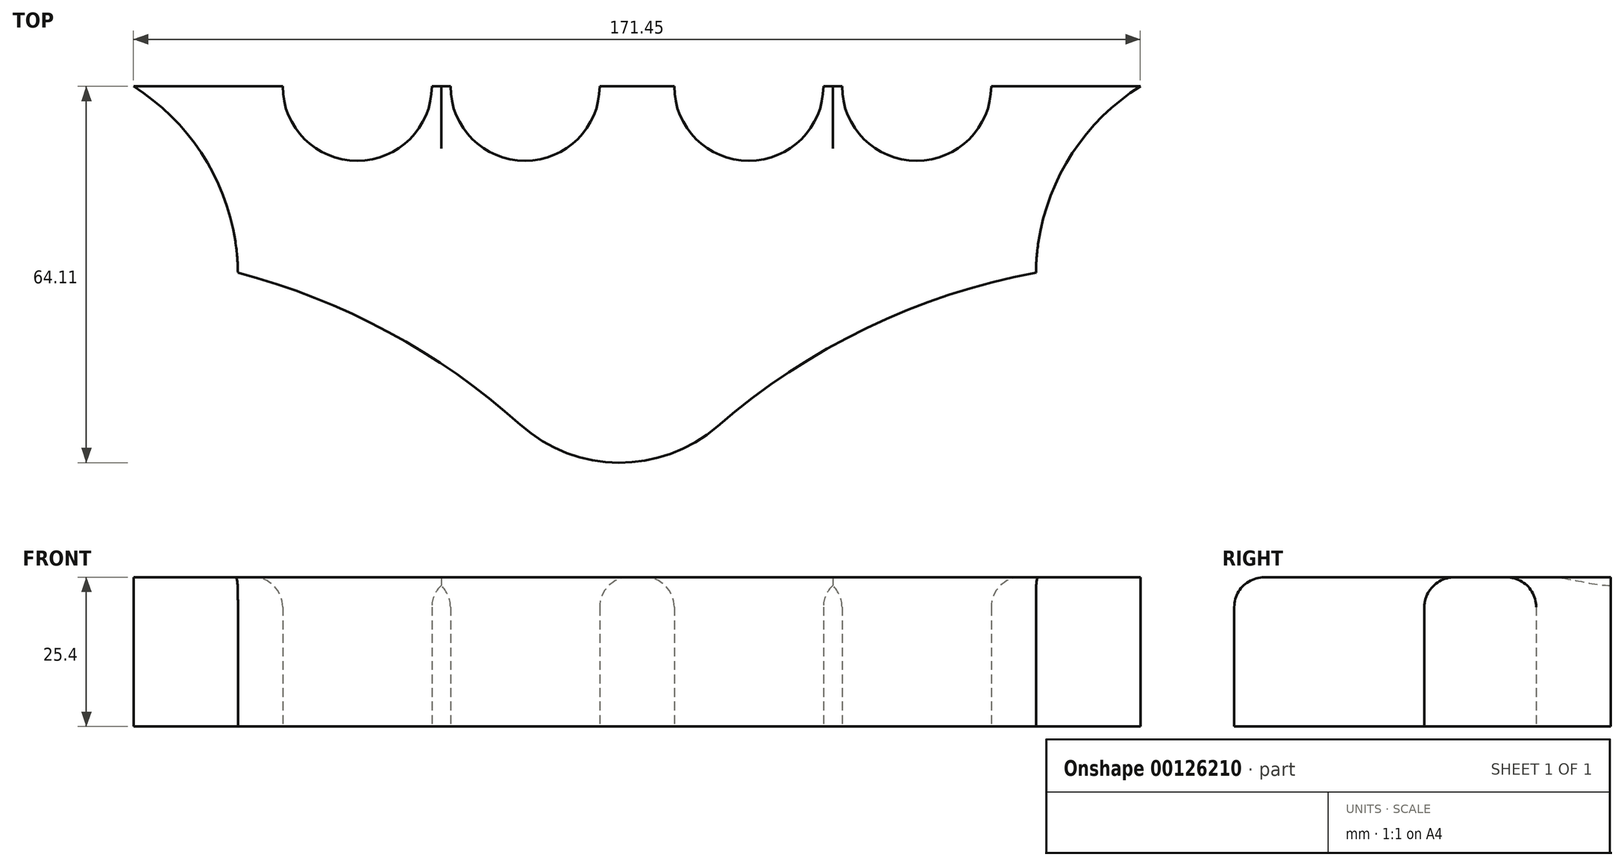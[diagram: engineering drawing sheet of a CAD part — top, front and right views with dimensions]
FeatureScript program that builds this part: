
annotation { "Feature Type Name" : "Feature", "Feature Type Description" : "" }
export const myFeature = defineFeature(function(context is Context, id is Id, definition is map)
    precondition{}
    {
        {
            var Q0;
            Q0=qCreatedBy(makeId("Top.planeOp"),FACE);
            var sketch = newSketch(context, id + "F0", { "sketchPlane" : qUnion([Q0])});
            skLineSegment(sketch, "E0", {"start": v(11.71, 92.4) * mm, "end": v(37.11, 92.4) * mm});
            skLineSegment(sketch, "E1", {"start": v(157.76, 92.4) * mm, "end": v(183.16, 92.4) * mm});
            skLineSegment(sketch, "E2", {"start": v(62.51, 92.4) * mm, "end": v(65.69, 92.4) * mm});
            skLineSegment(sketch, "E3", {"start": v(91.09, 92.4) * mm, "end": v(103.79, 92.4) * mm});
            skLineSegment(sketch, "E4", {"start": v(129.19, 92.4) * mm, "end": v(132.36, 92.4) * mm});
            skArc(sketch, "E5", {"start": v(37.11, 92.4) * mm, "mid": v(49.81, 79.7) * mm, "end": v(62.51, 92.4) * mm});
            skArc(sketch, "E6", {"start": v(65.69, 92.4) * mm, "mid": v(78.39, 79.7) * mm, "end": v(91.09, 92.4) * mm});
            skArc(sketch, "E7", {"start": v(103.79, 92.4) * mm, "mid": v(116.49, 79.7) * mm, "end": v(129.19, 92.4) * mm});
            skArc(sketch, "E8", {"start": v(132.36, 92.4) * mm, "mid": v(145.06, 79.7) * mm, "end": v(157.76, 92.4) * mm});
            skArc(sketch, "E9", {"start": v(29.5, 60.64) * mm, "mid": v(24.64, 78.78) * mm, "end": v(11.71, 92.4) * mm});
            skArc(sketch, "E10", {"start": v(94.26, 16.2) * mm, "mid": v(65.75, 44.06) * mm, "end": v(29.5, 60.64) * mm});
            skArc(sketch, "E11", {"start": v(183.16, 92.4) * mm, "mid": v(170.24, 78.78) * mm, "end": v(165.38, 60.64) * mm});
            skArc(sketch, "E12", {"start": v(165.38, 60.64) * mm, "mid": v(125.6, 45.18) * mm, "end": v(94.26, 16.2) * mm});
            skSolve(sketch);
        }
        {
            var Q0;
            Q0=makeQuery(id+"F0.imprint","IMPRINT",FACE,{"disambiguationData":[TD([[makeQuery(id+"F0.imprint","IMPRINT",EDGE,{"derivedFrom":sQuery(id+"F0.wireOp",EDGE,"E0")}),-1.0]])]});
            extrude(context, id + "F1", {"entities" : qUnion([Q0]), "depth" : 25.4 * mm});
        }
        {
            var Q0;
            Q0=makeQuery(id+"F1.opExtrude","SWEPT_EDGE",EDGE,{"disambiguationData":[OSD([sQuery(id+"F0.wireOp",EDGE,"E10"),sQuery(id+"F0.wireOp",EDGE,"E12")])]});
            fillet(context, id + "F2", {"entities" : qUnion([Q0]), "radius" : 25.4 * mm, "tangentPropagation" : true, "allowEdgeOverflow" : false});
        }
        {
            var Q0;
            Q0=makeQuery(id+"F1.opExtrude","CAP_EDGE",EDGE,{"disambiguationData":[OSD([sQuery(id+"F0.wireOp",EDGE,"E5")])],"isStart":false});
            var Q1;
            Q1=makeQuery(id+"F1.opExtrude","CAP_EDGE",EDGE,{"disambiguationData":[OSD([sQuery(id+"F0.wireOp",EDGE,"E7")])],"isStart":false});
            var Q2;
            Q2=makeQuery(id+"F1.opExtrude","CAP_EDGE",EDGE,{"disambiguationData":[OSD([sQuery(id+"F0.wireOp",EDGE,"E8")])],"isStart":false});
            var Q3;
            Q3=makeQuery(id+"F1.opExtrude","CAP_EDGE",EDGE,{"disambiguationData":[OSD([sQuery(id+"F0.wireOp",EDGE,"E6")])],"isStart":false});
            fillet(context, id + "F3", {"entities" : qUnion([Q0, Q1, Q2, Q3]), "radius" : 5.08 * mm, "tangentPropagation" : true, "allowEdgeOverflow" : false});
        }
        {
            var Q0;
            {var subQ0=sQuery(id+"F0.wireOp",EDGE,"E12");var subQ1=sQuery(id+"F0.wireOp",EDGE,"E10");Q0=makeQuery(id+"F2.opFillet","BLEND_EDGE",EDGE,{"blendedFrom":[makeQuery(id+"F1.opExtrude","SWEPT_EDGE",EDGE,{"disambiguationData":[OSD([subQ1,subQ0])]}),makeQuery(id+"F1.opExtrude","CAP_FACE",FACE,{"disambiguationData":[OSD([sQuery(id+"F0.wireOp",EDGE,"E0"),sQuery(id+"F0.wireOp",EDGE,"E1"),sQuery(id+"F0.wireOp",EDGE,"E2"),sQuery(id+"F0.wireOp",EDGE,"E3"),sQuery(id+"F0.wireOp",EDGE,"E4"),sQuery(id+"F0.wireOp",EDGE,"E5"),sQuery(id+"F0.wireOp",EDGE,"E6"),sQuery(id+"F0.wireOp",EDGE,"E7"),sQuery(id+"F0.wireOp",EDGE,"E8"),sQuery(id+"F0.wireOp",EDGE,"E9"),subQ1,sQuery(id+"F0.wireOp",EDGE,"E11"),subQ0])],"isStart":false})],"blendedInto":[makeQuery(id+"F1.opExtrude","CAP_FACE",FACE,{"disambiguationData":[OSD([sQuery(id+"F0.wireOp",EDGE,"E0"),sQuery(id+"F0.wireOp",EDGE,"E1"),sQuery(id+"F0.wireOp",EDGE,"E2"),sQuery(id+"F0.wireOp",EDGE,"E3"),sQuery(id+"F0.wireOp",EDGE,"E4"),sQuery(id+"F0.wireOp",EDGE,"E5"),sQuery(id+"F0.wireOp",EDGE,"E6"),sQuery(id+"F0.wireOp",EDGE,"E7"),sQuery(id+"F0.wireOp",EDGE,"E8"),sQuery(id+"F0.wireOp",EDGE,"E9"),subQ1,sQuery(id+"F0.wireOp",EDGE,"E11"),subQ0])],"isStart":false})]});}
            fillet(context, id + "F4", {"entities" : qUnion([Q0]), "radius" : 5.08 * mm, "tangentPropagation" : true, "allowEdgeOverflow" : false});
        }
        {
            var Q0;
            Q0=makeQuery(id+"F1.opExtrude","SWEPT_BODY",BODY,{"disambiguationData":[OSD([sQuery(id+"F0.wireOp",EDGE,"E0"),sQuery(id+"F0.wireOp",EDGE,"E1"),sQuery(id+"F0.wireOp",EDGE,"E2"),sQuery(id+"F0.wireOp",EDGE,"E3"),sQuery(id+"F0.wireOp",EDGE,"E4"),sQuery(id+"F0.wireOp",EDGE,"E5"),sQuery(id+"F0.wireOp",EDGE,"E6"),sQuery(id+"F0.wireOp",EDGE,"E7"),sQuery(id+"F0.wireOp",EDGE,"E8"),sQuery(id+"F0.wireOp",EDGE,"E9"),sQuery(id+"F0.wireOp",EDGE,"E10"),sQuery(id+"F0.wireOp",EDGE,"E11"),sQuery(id+"F0.wireOp",EDGE,"E12")])]});
            transform(context, id + "F5", {"entities" : qUnion([Q0]), "transformType" : TransformType.COPY});
        }
        {
            var Q0;
            Q0=makeQuery(id+"F5.opPattern","COPY",BODY,{"derivedFrom":makeQuery(id+"F1.opExtrude","SWEPT_BODY",BODY,{"disambiguationData":[OSD([sQuery(id+"F0.wireOp",EDGE,"E0"),sQuery(id+"F0.wireOp",EDGE,"E1"),sQuery(id+"F0.wireOp",EDGE,"E2"),sQuery(id+"F0.wireOp",EDGE,"E3"),sQuery(id+"F0.wireOp",EDGE,"E4"),sQuery(id+"F0.wireOp",EDGE,"E5"),sQuery(id+"F0.wireOp",EDGE,"E6"),sQuery(id+"F0.wireOp",EDGE,"E7"),sQuery(id+"F0.wireOp",EDGE,"E8"),sQuery(id+"F0.wireOp",EDGE,"E9"),sQuery(id+"F0.wireOp",EDGE,"E10"),sQuery(id+"F0.wireOp",EDGE,"E11"),sQuery(id+"F0.wireOp",EDGE,"E12")])]}),"instanceName":"1"});
            var Q1;
            Q1=makeQuery(id+"F0.imprint","IMPRINT",FACE,{"disambiguationData":[TD([[makeQuery(id+"F0.imprint","IMPRINT",EDGE,{"derivedFrom":sQuery(id+"F0.wireOp",EDGE,"E0")}),-1.0]])]});
            transform(context, id + "F6", {"entities" : qUnion([Q0]), "transformType" : TransformType.TRANSLATION_DISTANCE, "transformDirection" : qUnion([Q1]), "distance" : 50.8 * mm, "oppositeDirection" : true, "makeCopy" : true});
        }
        {
            var Q0;
            Q0=makeQuery(id+"F5.opPattern","COPY",BODY,{"derivedFrom":makeQuery(id+"F1.opExtrude","SWEPT_BODY",BODY,{"disambiguationData":[OSD([sQuery(id+"F0.wireOp",EDGE,"E0"),sQuery(id+"F0.wireOp",EDGE,"E1"),sQuery(id+"F0.wireOp",EDGE,"E2"),sQuery(id+"F0.wireOp",EDGE,"E3"),sQuery(id+"F0.wireOp",EDGE,"E4"),sQuery(id+"F0.wireOp",EDGE,"E5"),sQuery(id+"F0.wireOp",EDGE,"E6"),sQuery(id+"F0.wireOp",EDGE,"E7"),sQuery(id+"F0.wireOp",EDGE,"E8"),sQuery(id+"F0.wireOp",EDGE,"E9"),sQuery(id+"F0.wireOp",EDGE,"E10"),sQuery(id+"F0.wireOp",EDGE,"E11"),sQuery(id+"F0.wireOp",EDGE,"E12")])]}),"instanceName":"1"});
            deleteBodies(context, id + "F7", {"entities" : qUnion([Q0])});
        }
        {
            var Q0;
            Q0=makeQuery(id+"F6.opPattern","COPY",BODY,{"derivedFrom":makeQuery(id+"F5.opPattern","COPY",BODY,{"derivedFrom":makeQuery(id+"F1.opExtrude","SWEPT_BODY",BODY,{"disambiguationData":[OSD([sQuery(id+"F0.wireOp",EDGE,"E0"),sQuery(id+"F0.wireOp",EDGE,"E1"),sQuery(id+"F0.wireOp",EDGE,"E2"),sQuery(id+"F0.wireOp",EDGE,"E3"),sQuery(id+"F0.wireOp",EDGE,"E4"),sQuery(id+"F0.wireOp",EDGE,"E5"),sQuery(id+"F0.wireOp",EDGE,"E6"),sQuery(id+"F0.wireOp",EDGE,"E7"),sQuery(id+"F0.wireOp",EDGE,"E8"),sQuery(id+"F0.wireOp",EDGE,"E9"),sQuery(id+"F0.wireOp",EDGE,"E10"),sQuery(id+"F0.wireOp",EDGE,"E11"),sQuery(id+"F0.wireOp",EDGE,"E12")])]}),"instanceName":"1"}),"instanceName":"1"});
            deleteBodies(context, id + "F8", {"entities" : qUnion([Q0])});
        }
    });
